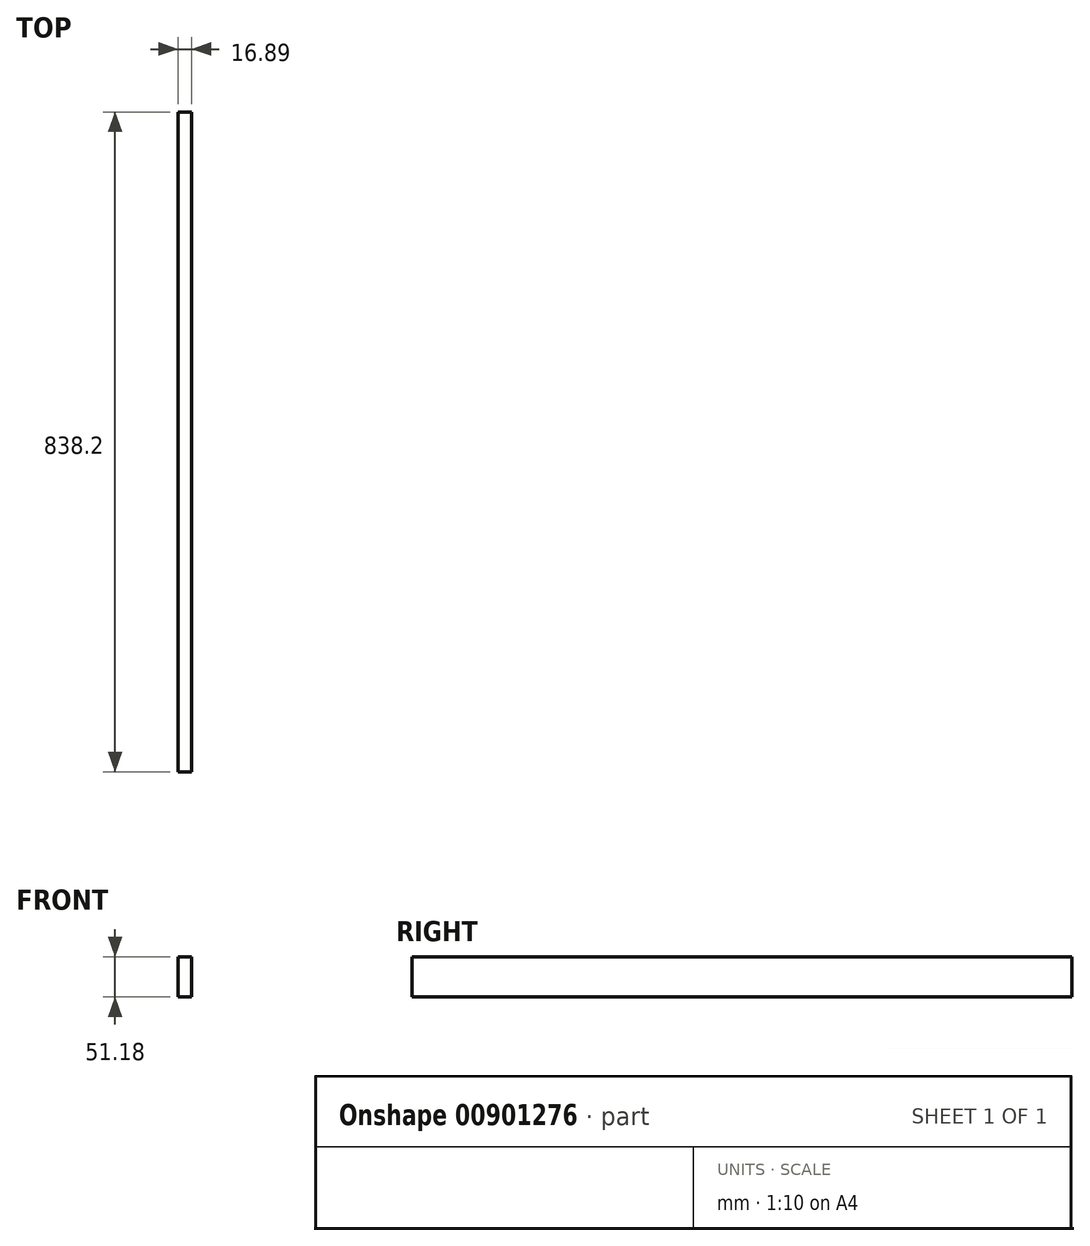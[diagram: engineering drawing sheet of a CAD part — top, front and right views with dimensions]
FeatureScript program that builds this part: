
annotation { "Feature Type Name" : "Feature", "Feature Type Description" : "" }
export const myFeature = defineFeature(function(context is Context, id is Id, definition is map)
    precondition{}
    {
        {
            var Q0;
            Q0=qCreatedBy(makeId("Right.planeOp"),FACE);
            var sketch = newSketch(context, id + "F0", { "sketchPlane" : qUnion([Q0])});
            skLineSegment(sketch, "E0.bottom", {"start": v(0, 0) * mm, "end": v(838.2, 0) * mm});
            skLineSegment(sketch, "E0.top", {"start": v(0, 51.18) * mm, "end": v(838.2, 51.18) * mm});
            skLineSegment(sketch, "E0.left", {"start": v(0, 0) * mm, "end": v(0, 51.18) * mm});
            skLineSegment(sketch, "E0.right", {"start": v(838.2, 0) * mm, "end": v(838.2, 51.18) * mm});
            skSolve(sketch);
        }
        {
            var Q0;
            Q0=qSketchRegion(id+"F0",true);
            extrude(context, id + "F1", {"entities" : qUnion([Q0]), "depth" : 16.9 * mm, "offsetDistance" : 25.4 * mm});
        }
    });
